# Revit family: HerzCon-узел прямого подключения для фанкойлов 65мм LF,MF
name_source: partatom
category: Rohrzubehör
units: mm (PartAtom-declared; Revit-internal decimal feet)

## family parameters
Arbeitsebenenbasiert = Nein
Beim Laden mit Abzugskörper schneiden = Nein
Bemaßung runder Anschluss = Durchmesser verwenden
Gemeinsam genutzt = Nein
Immer vertikal = Ja
OmniClass-Nummer = 23.65.55.14
OmniClass-Titel = Valves for Liquid Services
Teiletyp = Unterbricht

## types (2) — shared parameters
D01 = 13 mm
D02 = 16.5 mm  [stored 0.0541339 ft]
D03 = 14.5 mm  [stored 0.0475722 ft]
D04 = 10 mm  [stored 0.0328084 ft]
D05 = 16.75 mm  [stored 0.0549541 ft]
D06 = 20.5 mm  [stored 0.0672572 ft]
D07 = 7.5 mm  [stored 0.0246063 ft]
D10 = 13.5 mm  [stored 0.0442913 ft]
D11 = 10.75 mm  [stored 0.035269 ft]
D12 = 12 mm  [stored 0.0393701 ft]
H01 = 19.5 mm  [stored 0.0639764 ft]
H02 = 26.55 mm  [stored 0.0871063 ft]
H03 = 26 mm
H04 = 2.5 mm  [stored 0.0082021 ft]
H05 = 18.5 mm  [stored 0.0606955 ft]
H06 = 8 mm  [stored 0.0262467 ft]
H07 = 27.8 mm  [stored 0.0912073 ft]
H08 = 2 mm  [stored 0.00656168 ft]
H09 = 7.2 mm  [stored 0.023622 ft]
H10 = 2 mm  [stored 0.00656168 ft]
H11 = 58.8 mm  [stored 0.192913 ft]
H15 = 75 mm
H16 = 34 mm
Hersteller = HERZ Armaturen Ges.m.b.H.
ISO01 = 181 mm
ISO02 = 176 mm
ISO03 = 15 mm  [stored 0.0492126 ft]
ISO04 = 47 mm  [stored 0.154199 ft]
ISO05 = 49 mm  [stored 0.160761 ft]
ISO06 = 114 mm  [stored 0.374016 ft]
ISO07 = -47 mm  [stored -0.154199 ft]
ISO08 = 134 mm
ISOH01 = 50 mm  [stored 0.164042 ft]
ISOH02 = -38 mm  [stored -0.124672 ft]
ISOR01 = 17.5 mm  [stored 0.0574147 ft]
KombiH04 = 23.6 mm  [stored 0.0774278 ft]
L01 = 6 mm  [stored 0.019685 ft]
L02 = 5 mm  [stored 0.0164042 ft]
L03 = 7 mm  [stored 0.0229659 ft]
SCRNCODE = 05;04;04
SCRNSEQ = ARM;TYP_ARM="DURR";02
SFD02 = 18 mm  [stored 0.0590551 ft]
SFD03 = 13.5 mm  [stored 0.0442913 ft]
SFH03 = 32.5 mm  [stored 0.106627 ft]
SFH04 = 26 mm
SFH05 = 19.5 mm  [stored 0.0639764 ft]
SFL01 = 17 mm  [stored 0.0557743 ft]
SFL02 = 12.4 mm
SFR01 = 16.5 mm  [stored 0.0541339 ft]
SFR02 = 5.5 mm  [stored 0.0180446 ft]
URL = www.herz-armaturen.ru
WI00 = 45.00°
WI01 = 120.00°
Корпус = латунь, устойчивая к селективной цинковой коррозии
Макс. рабочая температура = 130 °C
Макс. рабочее давление = 2500000.0 Pa
Мембрана и уплотнительное кольцо O-Ring = EPDM
Мин. рабочая температура = -20 °C
Применение = HerzCON был разработан для простого подключения фанкойлов или AHU.
HerzCON - это устройство, состоящее из независимого от давления комби-клапана - регулятора расхода (4006), HERZ фильтра-грязевика, HERZ крана для слива (2512) и двух HERZ мультифункциональных шаровых кранов.
Включение, выключение и модульное управление возможно производить через приводы 0 - 10 В.
Приводы могут быть интегрированы в BMS при необходимости.
Устройство обеспечивает независимое от давления управление и в то же время гарантирует постоянный расход для конечного потребителя, максимизируя энергоэффективность системы.
Устройство HerzCON также позволяет производить промывку и запирание.
HerzCON предназначен для работы как в системах холодоснабжения, так и теплоснабжения.
Кран для слива, установленный на сетчатом фильтре, позволяет производить промывку устройства без необходимости извлечения сетчатого фильтра, а также позволяет очищать сетчатый фильтр в самом устройстве.
Среда = Вода для системы отопления подготавливается в соответствии с ÖNORM H5195 или VDI 2035.
Возможно использование этилена или пропиленгликоля в концентрации 25-50% объема.
Теплоизолирующий бокс = EPP, вспененный полипропилен, паронепроницаемый, антидиффузионный, черного цвета
Ход = 4 мм
zero-valued in all types: Vorgabe-Ansicht

## type names (no varying parameters)
- DN15 LF
- DN15 MF

note: [stored X ft] marks values corroborated as IEEE doubles in the binary element streams (Revit-internal decimal feet)
